# Revit family: BTD-L
name_source: partatom
category: Communication Devices
units: mm (PartAtom-declared; Revit-internal decimal feet)

## family parameters
Cut with Voids When Loaded = No
Host = Face
Maintain Annotation Orientation = No
OmniClass Number = 23.85.80.11.27
OmniClass Title = Lighting Controls
Part Type = Normal
Room Calculation Point = No
Round Connector Dimension = Use Diameter
Shared = Yes

## types (1)
- BTD
    Assembly Code = D5090
    Black = Paint - Carbon Black
    Default Elevation = 48 "
    Description = Control Solutions' specialty button service provides an easy, customized solution to meet commercial design requirements. The offering includes a list of our most popular text buttons and options to customize the text. Our custom service supports NX, CX and LVS wall stations. The buttons can easily be installed without the need to detach the switch from the wall. Custom text buttons are the ideal solution for any application providing unique control and a personalized experience. All custom specialty button orders require the appropriate product order form to be complted and attached to the order to ensure accuracy.
    Features = Easy to install
1-6 button models with or without light pipe for pilot light functionality
Available for all HCS wall station types: NXSW, CXSW and LVS
Available in White, Gray, Ivory, Light Almond, Black and Red
5pt Arial Narrow
8-character limit using capital letters
Order forms are product specific
Order forms provided to customer service must be in the original editable PDF downloaded from the HCS website (not scanned, handwritten, faxed and not a copy)
5-year warranty
    Light = Yes
    Manufacturer = NX Lighting Controls
    Model = Specialty Text Buttons
    Type Comments = Text Buttons
    URL = https://www.currentlighting.com
    White = Paint -  Matte White
    Width = 1.6 "

## geometry (parser evidence)
native form markers: Sweep x3
no freeform markers — native parametric forms only
